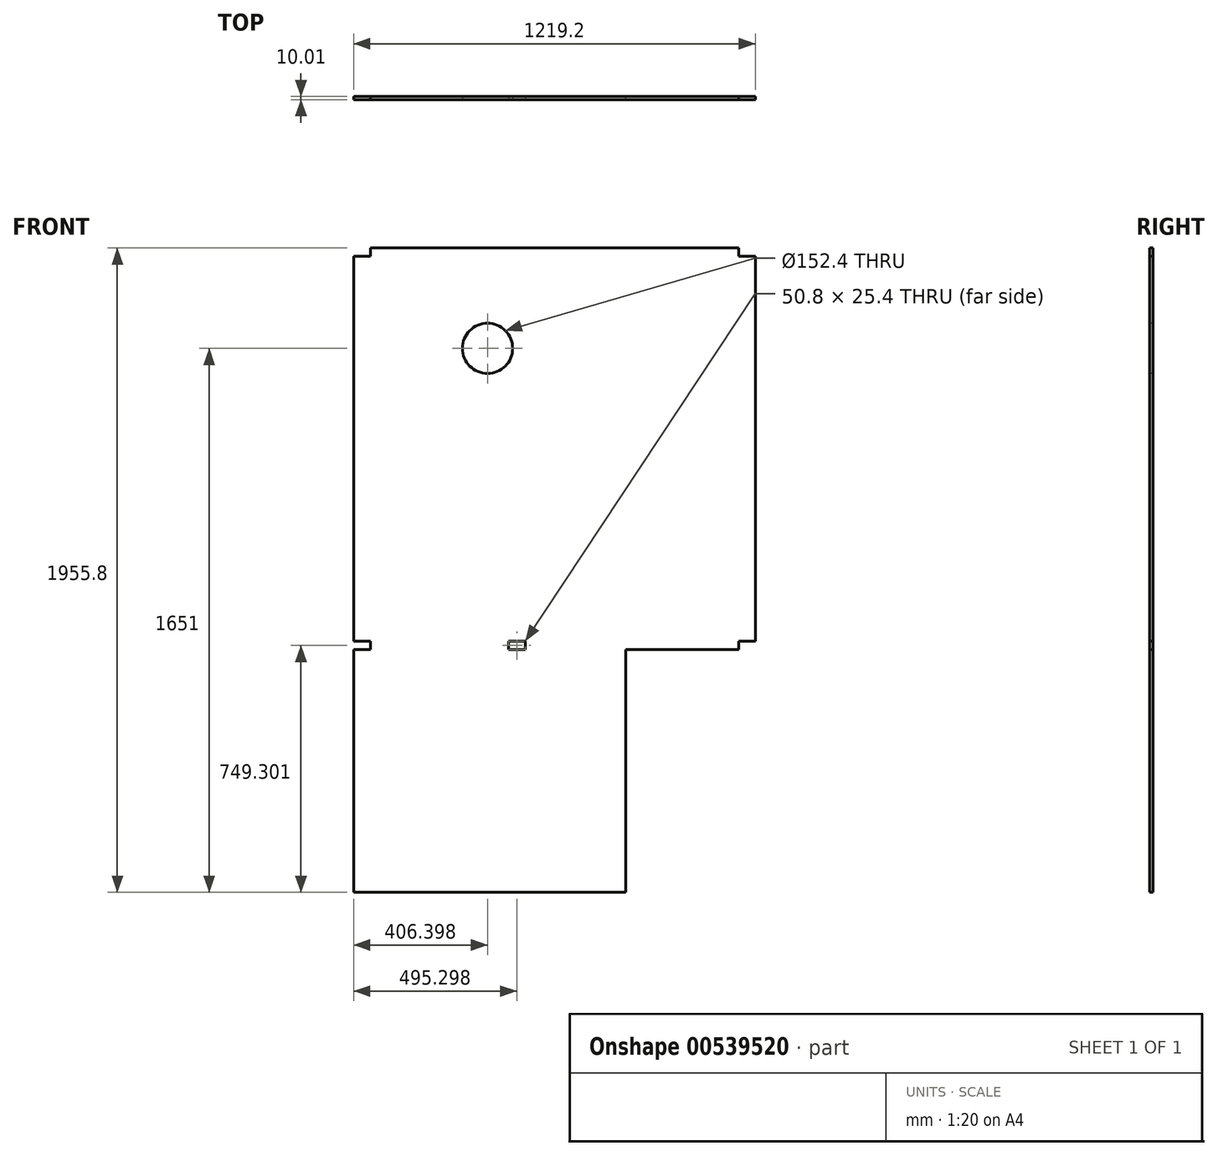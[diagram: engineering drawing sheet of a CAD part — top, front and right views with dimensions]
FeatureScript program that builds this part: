
annotation { "Feature Type Name" : "Feature", "Feature Type Description" : "" }
export const myFeature = defineFeature(function(context is Context, id is Id, definition is map)
    precondition{}
    {
        {
            var Q0;
            Q0=qCreatedBy(makeId("Front.planeOp"),FACE);
            var sketch = newSketch(context, id + "F0", { "sketchPlane" : qUnion([Q0])});
            skLineSegment(sketch, "E0", {"start": v(-507.77, 899.2) * mm, "end": v(711.43, 899.2) * mm});
            skLineSegment(sketch, "E1", {"start": v(711.43, 899.2) * mm, "end": v(711.43, -320) * mm});
            skLineSegment(sketch, "E2", {"start": v(711.43, -320) * mm, "end": v(317.73, -320) * mm});
            skLineSegment(sketch, "E3", {"start": v(317.73, -320) * mm, "end": v(317.73, -1056.6) * mm});
            skLineSegment(sketch, "E4", {"start": v(317.73, -1056.6) * mm, "end": v(-507.77, -1056.6) * mm});
            skLineSegment(sketch, "E5", {"start": v(-507.77, -1056.6) * mm, "end": v(-507.77, 899.2) * mm});
            skSolve(sketch);
        }
        {
            var Q0;
            Q0 = qSketchRegion(id + "F0", true);
            extrude(context, id + "F1", {"entities" : qUnion([Q0]), "depth" : 10 * mm, "offsetDistance" : 25.4 * mm});
        }
        {
            var Q0;
            Q0=makeQuery(id+"F1.opExtrude","CAP_FACE",FACE,{"disambiguationData":[OSD([sQuery(id+"F0.wireOp",EDGE,"E0"),sQuery(id+"F0.wireOp",EDGE,"E1"),sQuery(id+"F0.wireOp",EDGE,"E2"),sQuery(id+"F0.wireOp",EDGE,"E3"),sQuery(id+"F0.wireOp",EDGE,"E4"),sQuery(id+"F0.wireOp",EDGE,"E5")])],"isStart":false});
            var sketch = newSketch(context, id + "F2", { "sketchPlane" : qUnion([Q0])});
            skLineSegment(sketch, "E6.bottom", {"start": v(660.63, 873.8) * mm, "end": v(711.43, 873.8) * mm});
            skLineSegment(sketch, "E6.top", {"start": v(660.63, 899.2) * mm, "end": v(711.43, 899.2) * mm});
            skLineSegment(sketch, "E6.left", {"start": v(660.63, 873.8) * mm, "end": v(660.63, 899.2) * mm});
            skLineSegment(sketch, "E6.right", {"start": v(711.43, 873.8) * mm, "end": v(711.43, 899.2) * mm});
            skLineSegment(sketch, "E7.bottom", {"start": v(-456.97, 873.8) * mm, "end": v(-507.77, 873.8) * mm});
            skLineSegment(sketch, "E7.top", {"start": v(-456.97, 899.2) * mm, "end": v(-507.77, 899.2) * mm});
            skLineSegment(sketch, "E7.left", {"start": v(-456.97, 873.8) * mm, "end": v(-456.97, 899.2) * mm});
            skLineSegment(sketch, "E7.right", {"start": v(-507.77, 873.8) * mm, "end": v(-507.77, 899.2) * mm});
            skLineSegment(sketch, "E8.bottom", {"start": v(660.63, -294.6) * mm, "end": v(711.43, -294.6) * mm});
            skLineSegment(sketch, "E8.top", {"start": v(660.63, -320) * mm, "end": v(711.43, -320) * mm});
            skLineSegment(sketch, "E8.left", {"start": v(660.63, -294.6) * mm, "end": v(660.63, -320) * mm});
            skLineSegment(sketch, "E8.right", {"start": v(711.43, -294.6) * mm, "end": v(711.43, -320) * mm});
            skLineSegment(sketch, "E9.bottom", {"start": v(-507.77, -320) * mm, "end": v(-456.97, -320) * mm});
            skLineSegment(sketch, "E9.top", {"start": v(-507.77, -294.6) * mm, "end": v(-456.97, -294.6) * mm});
            skLineSegment(sketch, "E9.left", {"start": v(-507.77, -320) * mm, "end": v(-507.77, -294.6) * mm});
            skLineSegment(sketch, "E9.right", {"start": v(-456.97, -320) * mm, "end": v(-456.97, -294.6) * mm});
            skLineSegment(sketch, "E10.bottom", {"start": v(-37.87, -320) * mm, "end": v(12.93, -320) * mm});
            skLineSegment(sketch, "E10.top", {"start": v(-37.87, -294.6) * mm, "end": v(12.93, -294.6) * mm});
            skLineSegment(sketch, "E10.left", {"start": v(-37.87, -320) * mm, "end": v(-37.87, -294.6) * mm});
            skLineSegment(sketch, "E10.right", {"start": v(12.93, -320) * mm, "end": v(12.93, -294.6) * mm});
            skSolve(sketch);
        }
        {
            var Q0;
            Q0 = qSketchRegion(id + "F2", true);
            extrude(context, id + "F3", {"entities" : qUnion([Q0]), "operationType" : NewBodyOperationType.REMOVE, "endBound" : BoundingType.THROUGH_ALL, "oppositeDirection" : true, "depth" : 25.4 * mm, "offsetDistance" : 25.4 * mm});
        }
        {
            var Q0;
            Q0=makeQuery(id+"F1.opExtrude","CAP_FACE",FACE,{"disambiguationData":[OSD([sQuery(id+"F0.wireOp",EDGE,"E0"),sQuery(id+"F0.wireOp",EDGE,"E1"),sQuery(id+"F0.wireOp",EDGE,"E2"),sQuery(id+"F0.wireOp",EDGE,"E3"),sQuery(id+"F0.wireOp",EDGE,"E4"),sQuery(id+"F0.wireOp",EDGE,"E5")])],"isStart":false});
            var sketch = newSketch(context, id + "F4", { "sketchPlane" : qUnion([Q0])});
            skCircle(sketch, "E11", {"center": v(-101.37, 594.4) * mm, "radius": 76.2 * mm});
            skSolve(sketch);
        }
        {
            var Q0;
            Q0 = qSketchRegion(id + "F4", true);
            extrude(context, id + "F5", {"entities" : qUnion([Q0]), "operationType" : NewBodyOperationType.REMOVE, "endBound" : BoundingType.THROUGH_ALL, "oppositeDirection" : true, "depth" : 25.4 * mm, "offsetDistance" : 25.4 * mm});
        }
    });
